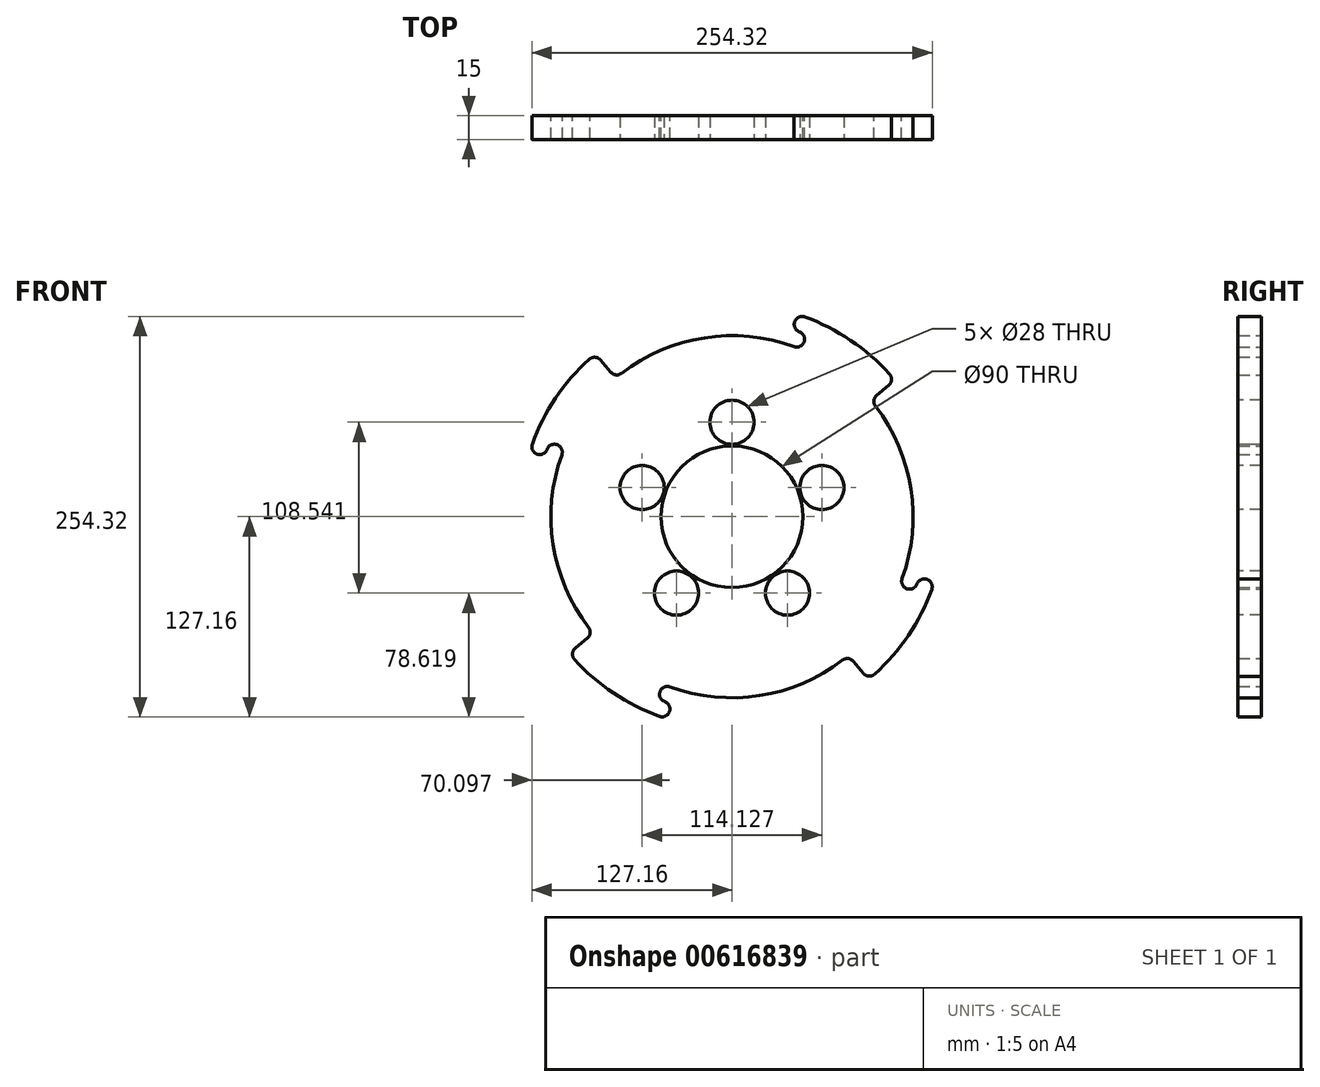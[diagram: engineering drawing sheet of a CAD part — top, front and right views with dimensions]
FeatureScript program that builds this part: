
annotation { "Feature Type Name" : "Feature", "Feature Type Description" : "" }
export const myFeature = defineFeature(function(context is Context, id is Id, definition is map)
    precondition{}
    {
        {
            var Q0;
            Q0=qCreatedBy(makeId("Front.planeOp"),FACE);
            var sketch = newSketch(context, id + "F0", { "sketchPlane" : qUnion([Q0])});
            skCircle(sketch, "E0", {"center": v(0, 0) * mm, "radius": 45 * mm});
            skCircle(sketch, "E1", {"center": v(0, 0) * mm, "radius": 60 * mm, "construction": true});
            skArc(sketch, "E2", {"start": v(-108.06, 39.33) * mm, "mid": v(-113.64, -17.6) * mm, "end": v(-91.1, -70.19) * mm});
            skArc(sketch, "E3", {"start": v(-90.69, 100) * mm, "mid": v(-112.05, 75.3) * mm, "end": v(-126.86, 46.17) * mm});
            skLineSegment(sketch, "E4", {"start": v(0, -160.96) * mm, "end": v(0, 165.3) * mm, "construction": true});
            skLineSegment(sketch, "E5", {"start": v(-181.36, 0) * mm, "end": v(230.59, 0) * mm, "construction": true});
            skLineSegment(sketch, "E6", {"start": v(0, 0) * mm, "end": v(-73.92, 88.1) * mm, "construction": true});
            skCircle(sketch, "E7", {"center": v(0, 60) * mm, "radius": 14 * mm});
            skCircle(sketch, "E8.1.0", {"center": v(-57.06, 18.54) * mm, "radius": 14 * mm});
            skCircle(sketch, "E8.2.0", {"center": v(-35.27, -48.54) * mm, "radius": 14 * mm});
            skCircle(sketch, "E8.3.0", {"center": v(35.27, -48.54) * mm, "radius": 14 * mm});
            skCircle(sketch, "E8.4.0", {"center": v(57.06, 18.54) * mm, "radius": 14 * mm});
            skLineSegment(sketch, "E9", {"start": v(0, 0) * mm, "end": v(-172.3, 62.71) * mm, "construction": true});
            skLineSegment(sketch, "E10", {"start": v(-77.07, 91.85) * mm, "end": v(-83.5, 99.51) * mm});
            skArc(sketch, "E11", {"start": v(-126.86, 46.17) * mm, "mid": v(-123.87, 39.76) * mm, "end": v(-117.46, 42.75) * mm});
            skArc(sketch, "E12", {"start": v(-108.06, 39.33) * mm, "mid": v(-111.05, 45.74) * mm, "end": v(-117.46, 42.75) * mm});
            skArc(sketch, "E13.1.0", {"start": v(-39.33, -108.06) * mm, "mid": v(-45.74, -111.05) * mm, "end": v(-42.75, -117.46) * mm});
            skArc(sketch, "E13.1.1", {"start": v(-46.17, -126.86) * mm, "mid": v(-39.76, -123.87) * mm, "end": v(-42.75, -117.46) * mm});
            skLineSegment(sketch, "E13.1.2", {"start": v(-91.85, -77.07) * mm, "end": v(-99.51, -83.5) * mm});
            skArc(sketch, "E13.2.0", {"start": v(108.06, -39.33) * mm, "mid": v(111.05, -45.74) * mm, "end": v(117.46, -42.75) * mm});
            skArc(sketch, "E13.2.1", {"start": v(126.86, -46.17) * mm, "mid": v(123.87, -39.76) * mm, "end": v(117.46, -42.75) * mm});
            skLineSegment(sketch, "E13.2.2", {"start": v(77.07, -91.85) * mm, "end": v(83.5, -99.51) * mm});
            skArc(sketch, "E13.3.0", {"start": v(39.33, 108.06) * mm, "mid": v(45.74, 111.05) * mm, "end": v(42.75, 117.46) * mm});
            skArc(sketch, "E13.3.1", {"start": v(46.17, 126.86) * mm, "mid": v(39.76, 123.87) * mm, "end": v(42.75, 117.46) * mm});
            skLineSegment(sketch, "E13.3.2", {"start": v(91.85, 77.07) * mm, "end": v(99.51, 83.5) * mm});
            skLineSegment(sketch, "E14.trimOffspring", {"start": v(-86.78, 103.42) * mm, "end": v(-114.3, 136.21) * mm, "construction": true});
            skArc(sketch, "E15.trimOffspring", {"start": v(100, 90.69) * mm, "mid": v(75.3, 112.05) * mm, "end": v(46.17, 126.86) * mm});
            skArc(sketch, "E16.trimOffspring", {"start": v(90.69, -100) * mm, "mid": v(112.05, -75.3) * mm, "end": v(126.86, -46.17) * mm});
            skArc(sketch, "E17.trimOffspring", {"start": v(-100, -90.69) * mm, "mid": v(-75.3, -112.05) * mm, "end": v(-46.17, -126.86) * mm});
            skPoint(sketch, "E18.visualSharp", {"position": v(-86.78, 103.42) * mm});
            skArc(sketch, "E18.filletArc", {"start": v(-83.5, 99.51) * mm, "mid": v(-87, 101.29) * mm, "end": v(-90.69, 100) * mm});
            skArc(sketch, "E19.trimOffspring", {"start": v(39.33, 108.06) * mm, "mid": v(-17.6, 113.64) * mm, "end": v(-70.19, 91.1) * mm});
            skArc(sketch, "E20.trimOffspring", {"start": v(108.06, -39.33) * mm, "mid": v(113.64, 17.6) * mm, "end": v(91.1, 70.19) * mm});
            skArc(sketch, "E21.trimOffspring", {"start": v(-39.33, -108.06) * mm, "mid": v(17.6, -113.64) * mm, "end": v(70.19, -91.1) * mm});
            skPoint(sketch, "E22.visualSharp", {"position": v(-73.92, 88.1) * mm});
            skArc(sketch, "E22.filletArc", {"start": v(-77.07, 91.85) * mm, "mid": v(-73.78, 90.09) * mm, "end": v(-70.19, 91.1) * mm});
            skPoint(sketch, "E23.visualSharp", {"position": v(-88.1, -73.92) * mm});
            skArc(sketch, "E23.filletArc", {"start": v(-91.85, -77.07) * mm, "mid": v(-90.09, -73.78) * mm, "end": v(-91.1, -70.19) * mm});
            skPoint(sketch, "E24.visualSharp", {"position": v(-103.42, -86.78) * mm});
            skArc(sketch, "E24.filletArc", {"start": v(-99.51, -83.5) * mm, "mid": v(-101.29, -87) * mm, "end": v(-100, -90.69) * mm});
            skPoint(sketch, "E25.visualSharp", {"position": v(73.92, -88.1) * mm});
            skArc(sketch, "E25.filletArc", {"start": v(77.07, -91.85) * mm, "mid": v(73.78, -90.09) * mm, "end": v(70.19, -91.1) * mm});
            skPoint(sketch, "E26.visualSharp", {"position": v(86.78, -103.42) * mm});
            skArc(sketch, "E26.filletArc", {"start": v(83.5, -99.51) * mm, "mid": v(87, -101.29) * mm, "end": v(90.69, -100) * mm});
            skPoint(sketch, "E27.visualSharp", {"position": v(103.42, 86.78) * mm});
            skArc(sketch, "E27.filletArc", {"start": v(99.51, 83.5) * mm, "mid": v(101.29, 87) * mm, "end": v(100, 90.69) * mm});
            skPoint(sketch, "E28.visualSharp", {"position": v(88.1, 73.92) * mm});
            skArc(sketch, "E28.filletArc", {"start": v(91.85, 77.07) * mm, "mid": v(90.09, 73.78) * mm, "end": v(91.1, 70.19) * mm});
            skLineSegment(sketch, "E29", {"start": v(0, 0) * mm, "end": v(-35.27, -48.54) * mm, "construction": true});
            skSolve(sketch);
        }
        {
            var Q0;
            Q0 = qSketchRegion(id + "F0", true);
            extrude(context, id + "F1", {"entities" : qUnion([Q0]), "depth" : 15 * mm, "offsetDistance" : 25 * mm});
        }
        {
            var Q0;
            Q0=makeQuery(id+"F1.opExtrude","CAP_FACE",FACE,{"disambiguationData":[OSD([sQuery(id+"F0.wireOp",EDGE,"E0"),sQuery(id+"F0.wireOp",EDGE,"E2"),sQuery(id+"F0.wireOp",EDGE,"E3"),sQuery(id+"F0.wireOp",EDGE,"E7"),sQuery(id+"F0.wireOp",EDGE,"E8.1.0"),sQuery(id+"F0.wireOp",EDGE,"E8.2.0"),sQuery(id+"F0.wireOp",EDGE,"E8.3.0"),sQuery(id+"F0.wireOp",EDGE,"E8.4.0"),sQuery(id+"F0.wireOp",EDGE,"E10"),sQuery(id+"F0.wireOp",EDGE,"E11"),sQuery(id+"F0.wireOp",EDGE,"E12"),sQuery(id+"F0.wireOp",EDGE,"E13.1.0"),sQuery(id+"F0.wireOp",EDGE,"E13.1.1"),sQuery(id+"F0.wireOp",EDGE,"E13.1.2"),sQuery(id+"F0.wireOp",EDGE,"E13.2.0"),sQuery(id+"F0.wireOp",EDGE,"E13.2.1"),sQuery(id+"F0.wireOp",EDGE,"E13.2.2"),sQuery(id+"F0.wireOp",EDGE,"E13.3.0"),sQuery(id+"F0.wireOp",EDGE,"E13.3.1"),sQuery(id+"F0.wireOp",EDGE,"E13.3.2"),sQuery(id+"F0.wireOp",EDGE,"E15.trimOffspring"),sQuery(id+"F0.wireOp",EDGE,"E16.trimOffspring"),sQuery(id+"F0.wireOp",EDGE,"E17.trimOffspring"),sQuery(id+"F0.wireOp",EDGE,"E18.filletArc"),sQuery(id+"F0.wireOp",EDGE,"E19.trimOffspring"),sQuery(id+"F0.wireOp",EDGE,"E20.trimOffspring"),sQuery(id+"F0.wireOp",EDGE,"E21.trimOffspring"),sQuery(id+"F0.wireOp",EDGE,"E22.filletArc"),sQuery(id+"F0.wireOp",EDGE,"E23.filletArc"),sQuery(id+"F0.wireOp",EDGE,"E24.filletArc"),sQuery(id+"F0.wireOp",EDGE,"E25.filletArc"),sQuery(id+"F0.wireOp",EDGE,"E26.filletArc"),sQuery(id+"F0.wireOp",EDGE,"E27.filletArc"),sQuery(id+"F0.wireOp",EDGE,"E28.filletArc")])],"isStart":false});
            var sketch = newSketch(context, id + "F2", { "sketchPlane" : qUnion([Q0])});
            skCircle(sketch, "E30", {"center": v(-97.88, 77.75) * mm, "radius": 20 * mm, "construction": true});
            skCircle(sketch, "E31", {"center": v(0, 0) * mm, "radius": 145 * mm, "construction": true});
            skLineSegment(sketch, "E32", {"start": v(-97.88, 77.75) * mm, "end": v(0, 0) * mm, "construction": true});
            skCircle(sketch, "E33.1.0", {"center": v(-77.75, -97.88) * mm, "radius": 20 * mm, "construction": true});
            skCircle(sketch, "E33.2.0", {"center": v(97.88, -77.75) * mm, "radius": 20 * mm, "construction": true});
            skCircle(sketch, "E33.3.0", {"center": v(77.75, 97.88) * mm, "radius": 20 * mm, "construction": true});
            skArc(sketch, "E34.0", {"start": v(-126.86, 46.17) * mm, "mid": v(-123.87, 39.76) * mm, "end": v(-117.46, 42.75) * mm, "construction": true});
            skSolve(sketch);
        }
        {
            var Q0;
            Q0=makeQuery(id+"FbXST540vmPBlkp_1.opExtrude","SWEPT_BODY",BODY,{"disambiguationData":[OSD([sQuery(id+"F2.wireOp",EDGE,"E30")])]});
            var Q1;
            Q1=makeQuery(id+"F1.opExtrude","SWEPT_BODY",BODY,{"disambiguationData":[OSD([sQuery(id+"F0.wireOp",EDGE,"E0"),sQuery(id+"F0.wireOp",EDGE,"E2"),sQuery(id+"F0.wireOp",EDGE,"E3"),sQuery(id+"F0.wireOp",EDGE,"E7"),sQuery(id+"F0.wireOp",EDGE,"E8.1.0"),sQuery(id+"F0.wireOp",EDGE,"E8.2.0"),sQuery(id+"F0.wireOp",EDGE,"E8.3.0"),sQuery(id+"F0.wireOp",EDGE,"E8.4.0"),sQuery(id+"F0.wireOp",EDGE,"E10"),sQuery(id+"F0.wireOp",EDGE,"E11"),sQuery(id+"F0.wireOp",EDGE,"E12"),sQuery(id+"F0.wireOp",EDGE,"E13.1.0"),sQuery(id+"F0.wireOp",EDGE,"E13.1.1"),sQuery(id+"F0.wireOp",EDGE,"E13.1.2"),sQuery(id+"F0.wireOp",EDGE,"E13.2.0"),sQuery(id+"F0.wireOp",EDGE,"E13.2.1"),sQuery(id+"F0.wireOp",EDGE,"E13.2.2"),sQuery(id+"F0.wireOp",EDGE,"E13.3.0"),sQuery(id+"F0.wireOp",EDGE,"E13.3.1"),sQuery(id+"F0.wireOp",EDGE,"E13.3.2"),sQuery(id+"F0.wireOp",EDGE,"E15.trimOffspring"),sQuery(id+"F0.wireOp",EDGE,"E16.trimOffspring"),sQuery(id+"F0.wireOp",EDGE,"E17.trimOffspring"),sQuery(id+"F0.wireOp",EDGE,"E18.filletArc"),sQuery(id+"F0.wireOp",EDGE,"E19.trimOffspring"),sQuery(id+"F0.wireOp",EDGE,"E20.trimOffspring"),sQuery(id+"F0.wireOp",EDGE,"E21.trimOffspring"),sQuery(id+"F0.wireOp",EDGE,"E22.filletArc"),sQuery(id+"F0.wireOp",EDGE,"E23.filletArc"),sQuery(id+"F0.wireOp",EDGE,"E24.filletArc"),sQuery(id+"F0.wireOp",EDGE,"E25.filletArc"),sQuery(id+"F0.wireOp",EDGE,"E26.filletArc"),sQuery(id+"F0.wireOp",EDGE,"E27.filletArc"),sQuery(id+"F0.wireOp",EDGE,"E28.filletArc")])]});
            var Q2;
            Q2=makeQuery(id+"F1.opExtrude","CAP_EDGE",EDGE,{"disambiguationData":[OSD([sQuery(id+"F0.wireOp",EDGE,"E0")])],"isStart":false});
            circularPattern(context, id + "F3", {"operationType" : NewBodyOperationType.ADD, "entities" : qUnion([Q0, Q1]), "axis" : qUnion([Q2]), "angle" : 360 * degree, "instanceCount" : 4, "equalSpace" : true, "computeTransformsWithoutBuiltin" : true});
        }
        {
            var Q0;
            Q0=makeQuery(id+"F1.opExtrude","CAP_FACE",FACE,{"disambiguationData":[OSD([sQuery(id+"F0.wireOp",EDGE,"E0"),sQuery(id+"F0.wireOp",EDGE,"E2"),sQuery(id+"F0.wireOp",EDGE,"E3"),sQuery(id+"F0.wireOp",EDGE,"E7"),sQuery(id+"F0.wireOp",EDGE,"E8.1.0"),sQuery(id+"F0.wireOp",EDGE,"E8.2.0"),sQuery(id+"F0.wireOp",EDGE,"E8.3.0"),sQuery(id+"F0.wireOp",EDGE,"E8.4.0"),sQuery(id+"F0.wireOp",EDGE,"E10"),sQuery(id+"F0.wireOp",EDGE,"E11"),sQuery(id+"F0.wireOp",EDGE,"E12"),sQuery(id+"F0.wireOp",EDGE,"E13.1.0"),sQuery(id+"F0.wireOp",EDGE,"E13.1.1"),sQuery(id+"F0.wireOp",EDGE,"E13.1.2"),sQuery(id+"F0.wireOp",EDGE,"E13.2.0"),sQuery(id+"F0.wireOp",EDGE,"E13.2.1"),sQuery(id+"F0.wireOp",EDGE,"E13.2.2"),sQuery(id+"F0.wireOp",EDGE,"E13.3.0"),sQuery(id+"F0.wireOp",EDGE,"E13.3.1"),sQuery(id+"F0.wireOp",EDGE,"E13.3.2"),sQuery(id+"F0.wireOp",EDGE,"E15.trimOffspring"),sQuery(id+"F0.wireOp",EDGE,"E16.trimOffspring"),sQuery(id+"F0.wireOp",EDGE,"E17.trimOffspring"),sQuery(id+"F0.wireOp",EDGE,"E18.filletArc"),sQuery(id+"F0.wireOp",EDGE,"E19.trimOffspring"),sQuery(id+"F0.wireOp",EDGE,"E20.trimOffspring"),sQuery(id+"F0.wireOp",EDGE,"E21.trimOffspring"),sQuery(id+"F0.wireOp",EDGE,"E22.filletArc"),sQuery(id+"F0.wireOp",EDGE,"E23.filletArc"),sQuery(id+"F0.wireOp",EDGE,"E24.filletArc"),sQuery(id+"F0.wireOp",EDGE,"E25.filletArc"),sQuery(id+"F0.wireOp",EDGE,"E26.filletArc"),sQuery(id+"F0.wireOp",EDGE,"E27.filletArc"),sQuery(id+"F0.wireOp",EDGE,"E28.filletArc")])],"isStart":false});
            var sketch = newSketch(context, id + "F4", { "sketchPlane" : qUnion([Q0])});
            skCircle(sketch, "E35", {"center": v(0, 0) * mm, "radius": 60 * mm, "construction": true});
            skCircle(sketch, "E36", {"center": v(0, 60) * mm, "radius": 14 * mm});
            skCircle(sketch, "E37.1.0", {"center": v(-57.06, 18.54) * mm, "radius": 14 * mm});
            skCircle(sketch, "E37.2.0", {"center": v(-35.27, -48.54) * mm, "radius": 14 * mm});
            skCircle(sketch, "E37.3.0", {"center": v(35.27, -48.54) * mm, "radius": 14 * mm});
            skCircle(sketch, "E37.4.0", {"center": v(57.06, 18.54) * mm, "radius": 14 * mm});
            skSolve(sketch);
        }
        {
            var Q0;
            Q0 = qSketchRegion(id + "F4", true);
            extrude(context, id + "F5", {"entities" : qUnion([Q0]), "operationType" : NewBodyOperationType.REMOVE, "endBound" : BoundingType.THROUGH_ALL, "oppositeDirection" : true, "depth" : 25 * mm, "offsetDistance" : 25 * mm});
        }
    });
